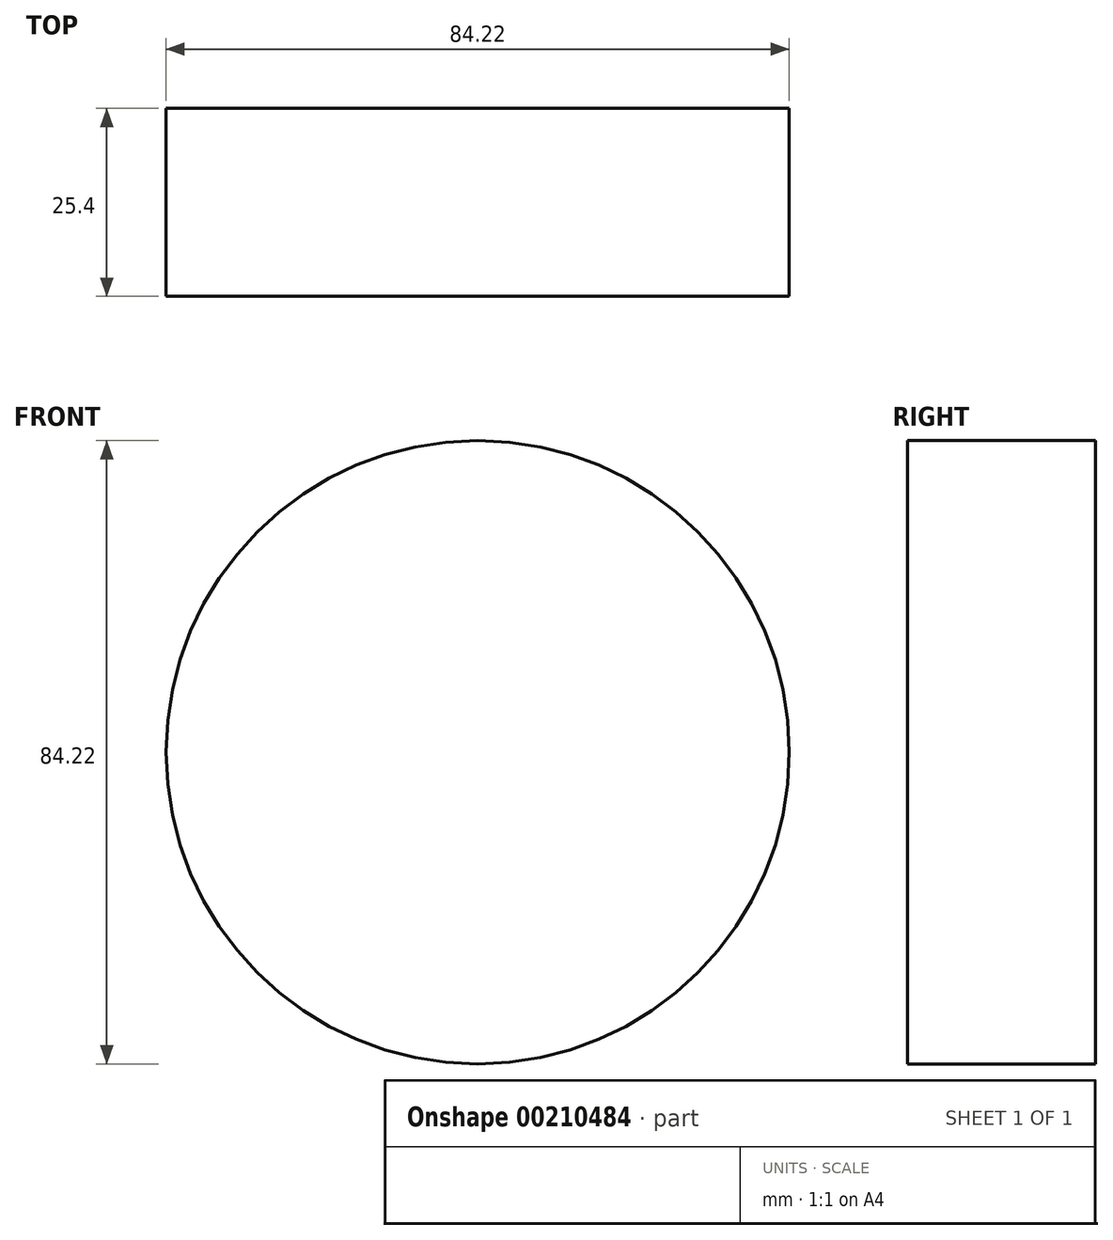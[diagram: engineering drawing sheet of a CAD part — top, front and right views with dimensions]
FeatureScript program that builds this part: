
annotation { "Feature Type Name" : "Feature", "Feature Type Description" : "" }
export const myFeature = defineFeature(function(context is Context, id is Id, definition is map)
    precondition{}
    {
        {
            var Q0;
            Q0=qCreatedBy(makeId("Front.planeOp"),FACE);
            var sketch = newSketch(context, id + "F0", { "sketchPlane" : qUnion([Q0])});
            skCircle(sketch, "E0", {"center": v(0, 0) * mm, "radius": 42.1 * mm});
            skSolve(sketch);
        }
        {
            var Q0;
            Q0 = qSketchRegion(id + "F0", true);
            extrude(context, id + "F1", {"entities" : qUnion([Q0]), "depth" : 25.4 * mm});
        }
    });
